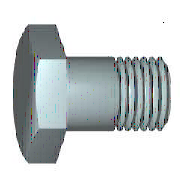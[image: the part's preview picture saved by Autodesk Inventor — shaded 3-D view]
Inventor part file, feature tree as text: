
AUTODESK INVENTOR PART (.ipt)
format: ipt  version: 2022 (Build 260153000, 153)  size: 190,464 bytes
history: native  units: mm (DEFAULTED — no unit token found)
features: sketch x3, extrude x1, chamfer x1, plane x1
ambient origin geometry x7: Origin, YZ Plane, XZ Plane, X Axis, Y Axis, Z Axis, Center Point
bodies: Solid1 (feature_tree), Body (feature_tree)
feature tree (6):
  extrude  "Head"  Depth=22.0mm
  chamfer  "Chamfer1"  Distance=4.7mm
  plane  "Work Plane1"
  sketch  "Sketch1"  dims[d0=65.0mm d1=22.0mm]
  sketch  "Sketch2"  dims[d2=8.0mm]
  sketch  "Sketch4"  dims[d12=90.0deg d3=4.7mm d4=0.0mm d5=30.0deg d21=90.0deg d6=0.766813mm d7=0.766912mm d8=0.0mm d9=0.6001mm d10=11.63mm d11=13.0mm d13=0.766912mm d14=8.0mm d15=22.0mm d16=0.0mm d19=13.0mm d55=45.0deg d57=0.0mm d58=0.0mm]
